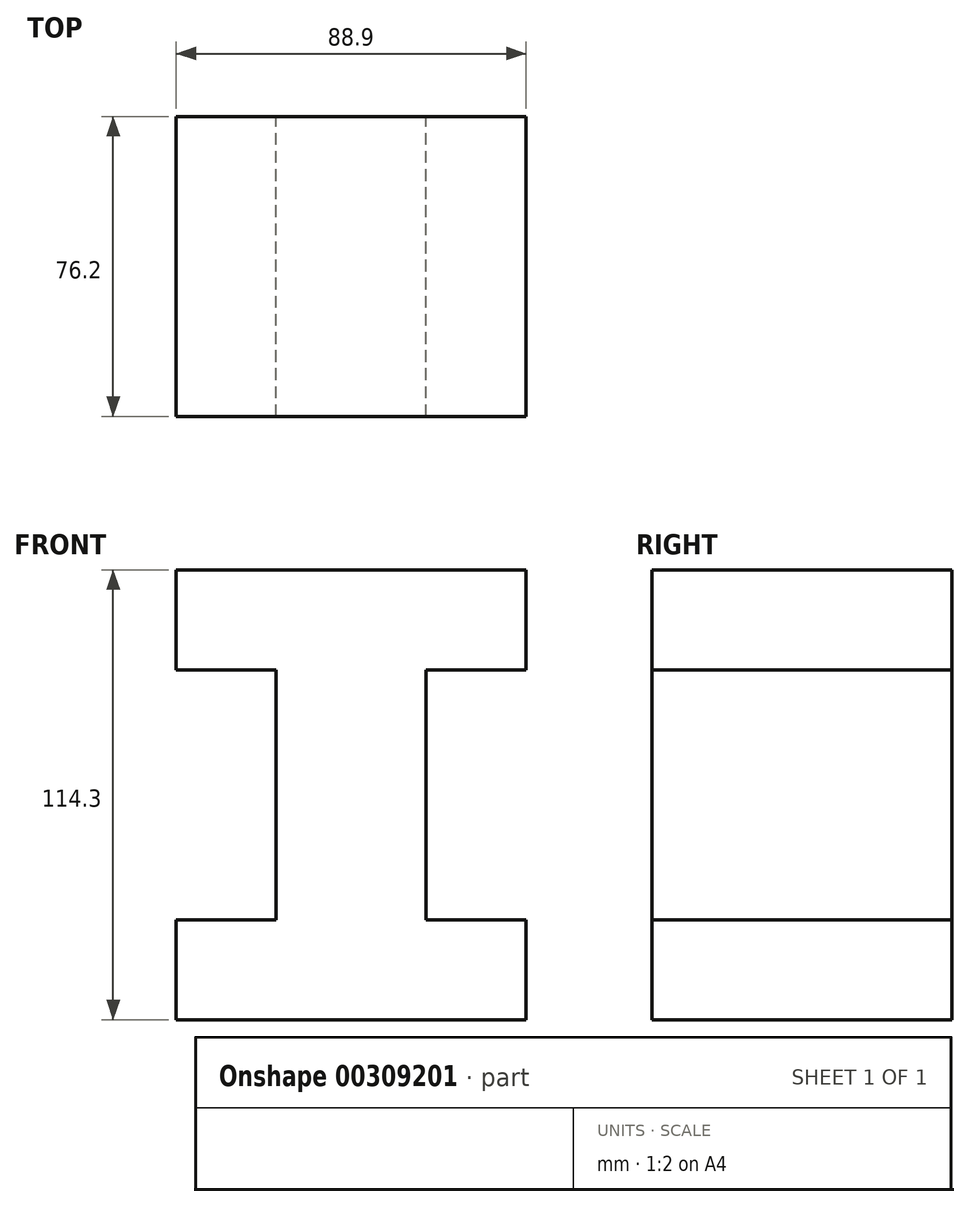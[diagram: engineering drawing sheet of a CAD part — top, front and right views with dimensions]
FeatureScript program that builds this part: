
annotation { "Feature Type Name" : "Feature", "Feature Type Description" : "" }
export const myFeature = defineFeature(function(context is Context, id is Id, definition is map)
    precondition{}
    {
        {
            var Q0;
            Q0=qCreatedBy(makeId("Front.planeOp"),FACE);
            var sketch = newSketch(context, id + "F0", { "sketchPlane" : qUnion([Q0])});
            skLineSegment(sketch, "E0", {"start": v(-45.89, 63.08) * mm, "end": v(43.01, 63.08) * mm});
            skLineSegment(sketch, "E1", {"start": v(43.01, 63.08) * mm, "end": v(43.01, 37.68) * mm});
            skLineSegment(sketch, "E2", {"start": v(43.01, 37.68) * mm, "end": v(17.61, 37.68) * mm});
            skLineSegment(sketch, "E3", {"start": v(17.61, 37.68) * mm, "end": v(17.61, -25.82) * mm});
            skLineSegment(sketch, "E4", {"start": v(17.61, -25.82) * mm, "end": v(43.01, -25.82) * mm});
            skLineSegment(sketch, "E5", {"start": v(43.01, -25.82) * mm, "end": v(43.01, -51.22) * mm});
            skLineSegment(sketch, "E6", {"start": v(43.01, -51.22) * mm, "end": v(-45.89, -51.22) * mm});
            skLineSegment(sketch, "E7", {"start": v(-45.89, -51.22) * mm, "end": v(-45.89, -25.82) * mm});
            skLineSegment(sketch, "E8", {"start": v(-45.89, -25.82) * mm, "end": v(-20.49, -25.82) * mm});
            skLineSegment(sketch, "E9", {"start": v(-20.49, -25.82) * mm, "end": v(-20.49, 37.68) * mm});
            skLineSegment(sketch, "E10", {"start": v(-20.49, 37.68) * mm, "end": v(-45.89, 37.68) * mm});
            skLineSegment(sketch, "E11", {"start": v(-45.89, 37.68) * mm, "end": v(-45.89, 63.08) * mm});
            skSolve(sketch);
        }
        {
            var Q0;
            Q0=makeQuery(id+"F0.imprint","IMPRINT",FACE,{"disambiguationData":[TD([[makeQuery(id+"F0.imprint","IMPRINT",EDGE,{"derivedFrom":sQuery(id+"F0.wireOp",EDGE,"E0")}),-1.0]])]});
            extrude(context, id + "F1", {"entities" : qUnion([Q0]), "depth" : 76.2 * mm});
        }
        {
            var Q0;
            Q0=makeQuery(id+"F1.opExtrude","CAP_FACE",FACE,{"disambiguationData":[OSD([sQuery(id+"F0.wireOp",EDGE,"E0"),sQuery(id+"F0.wireOp",EDGE,"E1"),sQuery(id+"F0.wireOp",EDGE,"E2"),sQuery(id+"F0.wireOp",EDGE,"E3"),sQuery(id+"F0.wireOp",EDGE,"E4"),sQuery(id+"F0.wireOp",EDGE,"E5"),sQuery(id+"F0.wireOp",EDGE,"E6"),sQuery(id+"F0.wireOp",EDGE,"E7"),sQuery(id+"F0.wireOp",EDGE,"E8"),sQuery(id+"F0.wireOp",EDGE,"E9"),sQuery(id+"F0.wireOp",EDGE,"E10"),sQuery(id+"F0.wireOp",EDGE,"E11")])],"isStart":false});
            var sketch = newSketch(context, id + "F2", { "sketchPlane" : qUnion([Q0])});
            skCircle(sketch, "E12.cCircle", {"center": v(0, 45.74) * mm, "radius": 7.65 * mm, "construction": true});
            skLineSegment(sketch, "E12.0", {"start": v(5.56, 38.1) * mm, "end": v(-5.56, 38.1) * mm});
            skLineSegment(sketch, "E12.1", {"start": v(-5.56, 38.1) * mm, "end": v(-9, 48.66) * mm});
            skLineSegment(sketch, "E12.2", {"start": v(-9, 48.66) * mm, "end": v(0, 55.2) * mm});
            skLineSegment(sketch, "E12.3", {"start": v(0, 55.2) * mm, "end": v(9, 48.66) * mm});
            skLineSegment(sketch, "E12.4", {"start": v(9, 48.66) * mm, "end": v(5.56, 38.1) * mm});
            skPoint(sketch, "E12.0.midPoint", {"position": v(0, 38.1) * mm});
            skSolve(sketch);
        }
        {
            var Q0;
            Q0=makeQuery(id+"F2.imprint","IMPRINT",FACE,{"disambiguationData":[TD([[makeQuery(id+"F2.imprint","IMPRINT",EDGE,{"derivedFrom":sQuery(id+"F2.wireOp",EDGE,"E12.0")}),-1.0]])]});
            extrude(context, id + "F3", {"entities" : qUnion([Q0]), "operationType" : NewBodyOperationType.REMOVE, "depth" : 25.4 * mm});
        }
    });
